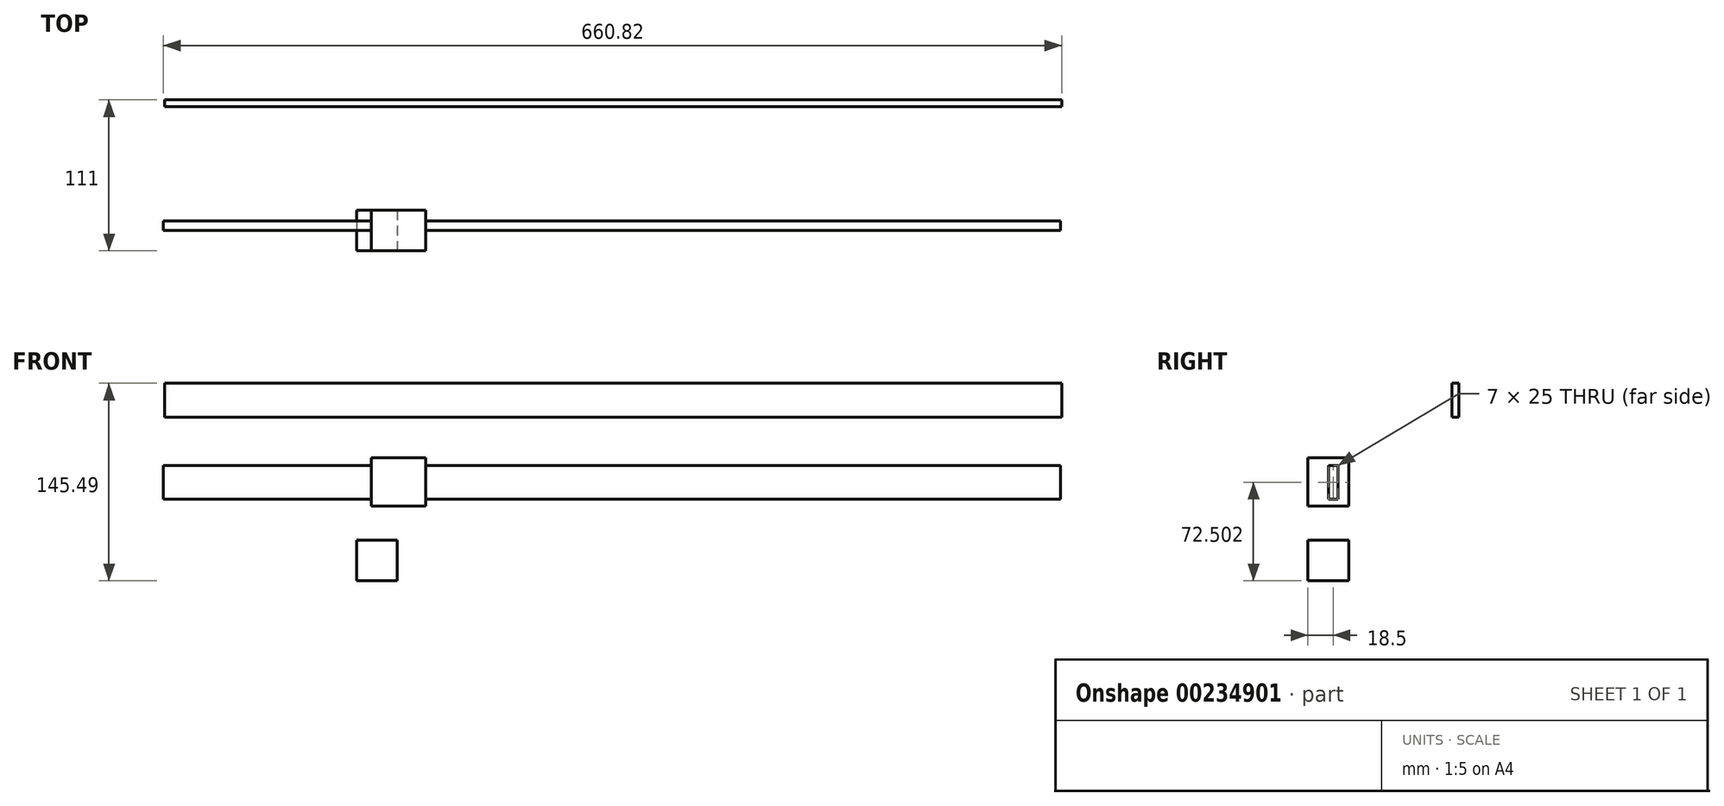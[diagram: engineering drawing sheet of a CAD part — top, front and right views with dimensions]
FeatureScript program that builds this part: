
annotation { "Feature Type Name" : "Feature", "Feature Type Description" : "" }
export const myFeature = defineFeature(function(context is Context, id is Id, definition is map)
    precondition{}
    {
        {
            var Q0;
            Q0=qCreatedBy(makeId("Front.planeOp"),FACE);
            var sketch = newSketch(context, id + "F0", { "sketchPlane" : qUnion([Q0])});
            skLineSegment(sketch, "E0.bottom", {"start": v(-330, 200.9) * mm, "end": v(330, 200.9) * mm});
            skLineSegment(sketch, "E0.top", {"start": v(-330, 175.9) * mm, "end": v(330, 175.9) * mm});
            skLineSegment(sketch, "E0.left", {"start": v(-330, 200.9) * mm, "end": v(-330, 175.9) * mm});
            skLineSegment(sketch, "E0.right", {"start": v(330, 200.9) * mm, "end": v(330, 175.9) * mm});
            skLineSegment(sketch, "E1.bottom", {"start": v(-180, 175.9) * mm, "end": v(-166, 175.9) * mm});
            skLineSegment(sketch, "E1.top", {"start": v(-180, 145.9) * mm, "end": v(-166, 145.9) * mm});
            skLineSegment(sketch, "E1.left", {"start": v(-180, 175.9) * mm, "end": v(-180, 145.9) * mm});
            skLineSegment(sketch, "E1.right", {"start": v(-166, 175.9) * mm, "end": v(-166, 145.9) * mm});
            skLineSegment(sketch, "E2.bottom", {"start": v(-188, 145.9) * mm, "end": v(-158, 145.9) * mm});
            skLineSegment(sketch, "E2.top", {"start": v(-188, 115.9) * mm, "end": v(-158, 115.9) * mm});
            skLineSegment(sketch, "E2.left", {"start": v(-188, 145.9) * mm, "end": v(-188, 115.9) * mm});
            skLineSegment(sketch, "E2.right", {"start": v(-158, 145.9) * mm, "end": v(-158, 115.9) * mm});
            skLineSegment(sketch, "E3.MirrorCS", {"start": v(188, 145.9) * mm, "end": v(158, 145.9) * mm});
            skLineSegment(sketch, "E4.MirrorCS", {"start": v(180, 175.9) * mm, "end": v(166, 175.9) * mm});
            skLineSegment(sketch, "E5.MirrorCS", {"start": v(180, 145.9) * mm, "end": v(166, 145.9) * mm});
            skLineSegment(sketch, "E6.MirrorCS", {"start": v(188, 145.9) * mm, "end": v(188, 115.9) * mm});
            skLineSegment(sketch, "E7.MirrorCS", {"start": v(188, 115.9) * mm, "end": v(158, 115.9) * mm});
            skLineSegment(sketch, "E8.MirrorCS", {"start": v(158, 145.9) * mm, "end": v(158, 115.9) * mm});
            skLineSegment(sketch, "E9.MirrorCS", {"start": v(180, 175.9) * mm, "end": v(180, 145.9) * mm});
            skLineSegment(sketch, "E10.MirrorCS", {"start": v(166, 175.9) * mm, "end": v(166, 145.9) * mm});
            skSolve(sketch);
        }
        {
            var Q0;
            Q0=makeQuery(id+"F0.imprint","IMPRINT",FACE,{"disambiguationData":[TD([[makeQuery(id+"F0.imprint","IMPRINT",EDGE,{"derivedFrom":sQuery(id+"F0.wireOp",EDGE,"E0.bottom")}),-1.0]])]});
            var Q1;
            Q1=makeQuery(id+"F0.imprint","IMPRINT",FACE,{"disambiguationData":[TD([[makeQuery(id+"F0.imprint","IMPRINT",EDGE,{"derivedFrom":sQuery(id+"F0.wireOp",EDGE,"E1.bottom")}),-1.0]])]});
            var Q2;
            Q2=makeQuery(id+"F0.imprint","IMPRINT",FACE,{"disambiguationData":[TD([[makeQuery(id+"F0.imprint","IMPRINT",EDGE,{"derivedFrom":sQuery(id+"F0.wireOp",EDGE,"E4.MirrorCS")}),1.0]])]});
            extrude(context, id + "F1", {"entities" : qUnion([Q0, Q1, Q2]), "oppositeDirection" : true, "depth" : 7 * mm});
        }
        {
            var Q0;
            Q0=makeQuery(id+"F0.imprint","IMPRINT",FACE,{"disambiguationData":[TD([[makeQuery(id+"F0.imprint","IMPRINT",EDGE,{"derivedFrom":sQuery(id+"F0.wireOp",EDGE,"E2.top")}),1.0]])]});
            var Q1;
            {var subQ0=sQuery(id+"F0.wireOp",EDGE,"E5.MirrorCS");Q1=makeQuery(id+"F0.imprint","IMPRINT",FACE,{"disambiguationData":[TD([[makeQuery(id+"F0.imprint","IMPRINT",EDGE,{"derivedFrom":subQ0}),1.0]])]});}
            extrude(context, id + "F2", {"entities" : qUnion([Q0, Q1]), "operationType" : NewBodyOperationType.ADD, "endBound" : BoundingType.SYMMETRIC, "oppositeDirection" : true, "depth" : 30 * mm});
        }
        {
            var Q0;
            Q0=qCreatedBy(makeId("Front.planeOp"),FACE);
            var sketch = newSketch(context, id + "F3", { "sketchPlane" : qUnion([Q0])});
            skLineSegment(sketch, "E11.bottom", {"start": v(-487.18, 261.38) * mm, "end": v(172.82, 261.38) * mm});
            skLineSegment(sketch, "E11.top", {"start": v(-487.18, 236.38) * mm, "end": v(172.82, 236.38) * mm});
            skLineSegment(sketch, "E11.left", {"start": v(-487.18, 261.38) * mm, "end": v(-487.18, 236.38) * mm});
            skLineSegment(sketch, "E11.right", {"start": v(172.82, 261.38) * mm, "end": v(172.82, 236.38) * mm});
            skLineSegment(sketch, "E12.MirrorCS", {"start": v(-150.18, 236.38) * mm, "end": v(-164.18, 236.38) * mm});
            skLineSegment(sketch, "E13.MirrorCS", {"start": v(-150.18, 236.38) * mm, "end": v(-150.18, 206.38) * mm});
            skLineSegment(sketch, "E14.MirrorCS", {"start": v(-164.18, 236.38) * mm, "end": v(-164.18, 206.38) * mm});
            skLineSegment(sketch, "E15", {"start": v(-164.18, 206.38) * mm, "end": v(-150.18, 206.38) * mm});
            skLineSegment(sketch, "E16.bottom", {"start": v(-177.18, 206.38) * mm, "end": v(-137.18, 206.38) * mm});
            skLineSegment(sketch, "E16.top", {"start": v(-177.18, 170.89) * mm, "end": v(-137.18, 170.89) * mm});
            skLineSegment(sketch, "E16.left", {"start": v(-177.18, 206.38) * mm, "end": v(-177.18, 170.89) * mm});
            skLineSegment(sketch, "E16.right", {"start": v(-137.18, 206.38) * mm, "end": v(-137.18, 170.89) * mm});
            skSolve(sketch);
        }
        {
            var Q0;
            Q0=makeQuery(id+"F3.imprint","IMPRINT",FACE,{"disambiguationData":[TD([[makeQuery(id+"F3.imprint","IMPRINT",EDGE,{"derivedFrom":sQuery(id+"F3.wireOp",EDGE,"E11.bottom")}),-1.0]])]});
            var Q1;
            Q1=makeQuery(id+"F3.imprint","IMPRINT",FACE,{"disambiguationData":[TD([[makeQuery(id+"F3.imprint","IMPRINT",EDGE,{"derivedFrom":sQuery(id+"F3.wireOp",EDGE,"E12.MirrorCS")}),1.0]])]});
            extrude(context, id + "F4", {"entities" : qUnion([Q0, Q1]), "oppositeDirection" : true, "depth" : 5 * mm});
        }
        {
            var Q0;
            Q0=makeQuery(id+"F3.imprint","IMPRINT",FACE,{"disambiguationData":[TD([[makeQuery(id+"F3.imprint","IMPRINT",EDGE,{"derivedFrom":sQuery(id+"F3.wireOp",EDGE,"E16.top")}),1.0]])]});
            extrude(context, id + "F5", {"entities" : qUnion([Q0]), "operationType" : NewBodyOperationType.ADD, "endBound" : BoundingType.SYMMETRIC, "depth" : 30 * mm});
        }
        {
            var Q0;
            Q0=makeQuery(id+"F4.opExtrude","SWEPT_BODY",BODY,{"disambiguationData":[OSD([sQuery(id+"F3.wireOp",EDGE,"E11.bottom"),sQuery(id+"F3.wireOp",EDGE,"E11.top"),sQuery(id+"F3.wireOp",EDGE,"E11.left"),sQuery(id+"F3.wireOp",EDGE,"E11.right"),sQuery(id+"F3.wireOp",EDGE,"E13.MirrorCS"),sQuery(id+"F3.wireOp",EDGE,"E14.MirrorCS"),sQuery(id+"F3.wireOp",EDGE,"E16.bottom")])]});
            transform(context, id + "F6", {"entities" : qUnion([Q0]), "transformType" : TransformType.TRANSLATION_3D, "dx" : 158 * mm, "dy" : 91 * mm, "dz" : 0 * mm, "makeCopy" : false});
        }
    });
